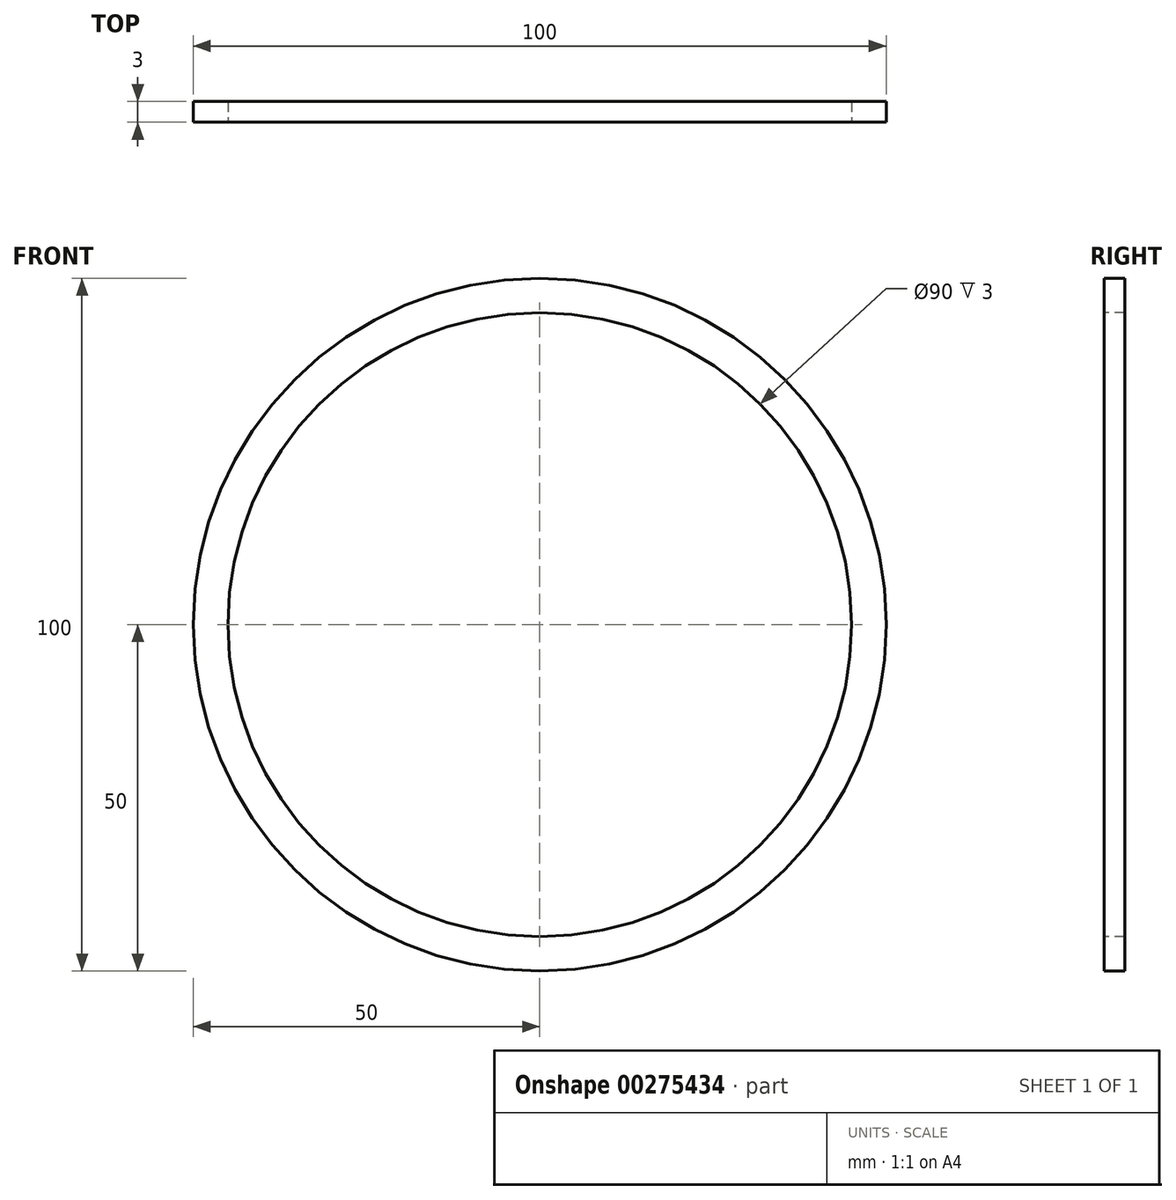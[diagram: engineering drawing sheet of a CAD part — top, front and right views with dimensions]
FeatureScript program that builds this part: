
annotation { "Feature Type Name" : "Feature", "Feature Type Description" : "" }
export const myFeature = defineFeature(function(context is Context, id is Id, definition is map)
    precondition{}
    {
        {
            var Q0;
            Q0=qCreatedBy(makeId("Front.planeOp"),FACE);
            var sketch = newSketch(context, id + "F0", { "sketchPlane" : qUnion([Q0])});
            skCircle(sketch, "E0", {"center": v(0, 0) * mm, "radius": 50 * mm});
            skSolve(sketch);
        }
        {
            var Q0;
            Q0 = qSketchRegion(id + "F0", true);
            extrude(context, id + "F1", {"entities" : qUnion([Q0]), "depth" : 3 * mm, "offsetDistance" : 25 * mm});
        }
        {
            var Q0;
            Q0=makeQuery(id+"F1.opExtrude","CAP_FACE",FACE,{"disambiguationData":[OSD([sQuery(id+"F0.wireOp",EDGE,"E0")])],"isStart":false});
            var sketch = newSketch(context, id + "F2", { "sketchPlane" : qUnion([Q0])});
            skCircle(sketch, "E1", {"center": v(0, 0) * mm, "radius": 45 * mm});
            skSolve(sketch);
        }
        {
            var Q0;
            Q0 = qSketchRegion(id + "F2", true);
            extrude(context, id + "F3", {"entities" : qUnion([Q0]), "operationType" : NewBodyOperationType.REMOVE, "oppositeDirection" : true, "depth" : 83 * mm, "offsetDistance" : 25 * mm});
        }
    });
